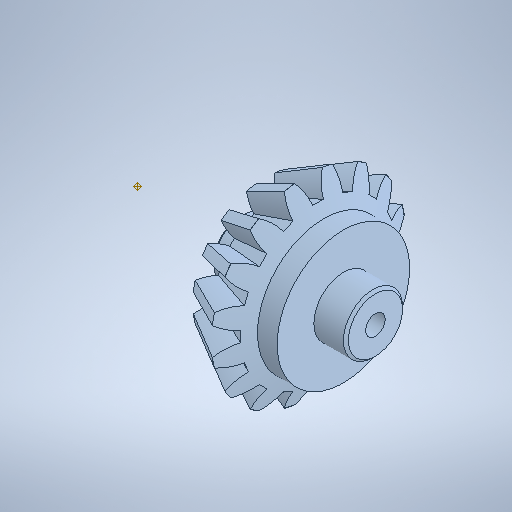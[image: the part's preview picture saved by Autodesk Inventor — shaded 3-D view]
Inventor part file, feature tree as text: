
AUTODESK INVENTOR PART (.ipt)
format: ipt  version: 2025.1 (Build 291241000, 241)  size: 506,880 bytes
history: native  units: in
note: dims shown in document units (in); Inventor stores cm internally (conversion verified against a paired STEP export)
features: plane x6, sketch x6, revolve x2, extrude x2, pattern_circular x1, chamfer x1, hole x1
ambient origin geometry x8: Origin, YZ Plane, XZ Plane, XY Plane, X Axis, Y Axis, Z Axis, Center Point
bodies: Solid1 (feature_tree)
feature tree (19):
  revolve  "Revolution1"  [1 undecoded]
  plane  "Work Plane2"
  plane  "Work Plane5"
  extrude  "Extrusion6"  Depth=0.0787in
  pattern_circular  "Circular Pattern2"  Count=4  [1 undecoded]
  plane  "Work Plane7"
  plane  "Work Plane6"
  sketch  "Sketch11"  dims[d5=0.3937in d9=1.5748in]
  revolve  "Revolution3"  [1 undecoded]
  extrude  "Extrusion8"  Depth=0.2362in
  chamfer  "Chamfer3"  Distance=1.4961in
  hole  "Perçage1"  [1 undecoded]
  sketch  "Sketch1"  dims[d0=3.1496in d1=0.1825in]
  plane  "Work Plane1"
  plane  "Work Plane4"
  sketch  "Sketch8"  dims[d2=0.0787in d3=0.0945in]
  sketch  "Sketch12"  dims[d10=90.0deg d11=0.162in d12=1.5748in]
  sketch  "Sketch13"  dims[d43=0.7043in d47=1.4085in d48=1.4961in d49=0.3543in d50=-0.4359in d51=1.5748in d53=0.0787in d54=0.0691in d56=0.4724in d57=-0.0197in d58=6.2992in d59=360.0deg d63=0.1297in d82=0.0875in d83=-0.0875in d84=1.4086in d89=0.2559in d90=0.315in d91=0.1181in d92=360.0deg d93=0.4567in d94=0.1969in d95=0.0in d96=0.2362in d105=0.0197in d106=0.0787in d107=45.0deg d130=0.1575in d131=0.5292in d132=0.1575in d133=0.2362in d134=0.1575in d135=0.0787in d136=90.0deg d137=0.2362in d138=0.8108in d139=0.1181in]
  sketch  "Esquisse20"
note: 4 required parameter values undecoded (feature->parameter linkage not recoverable at this tier; creation-order binding heuristic only, values carry confidence <= 0.55)